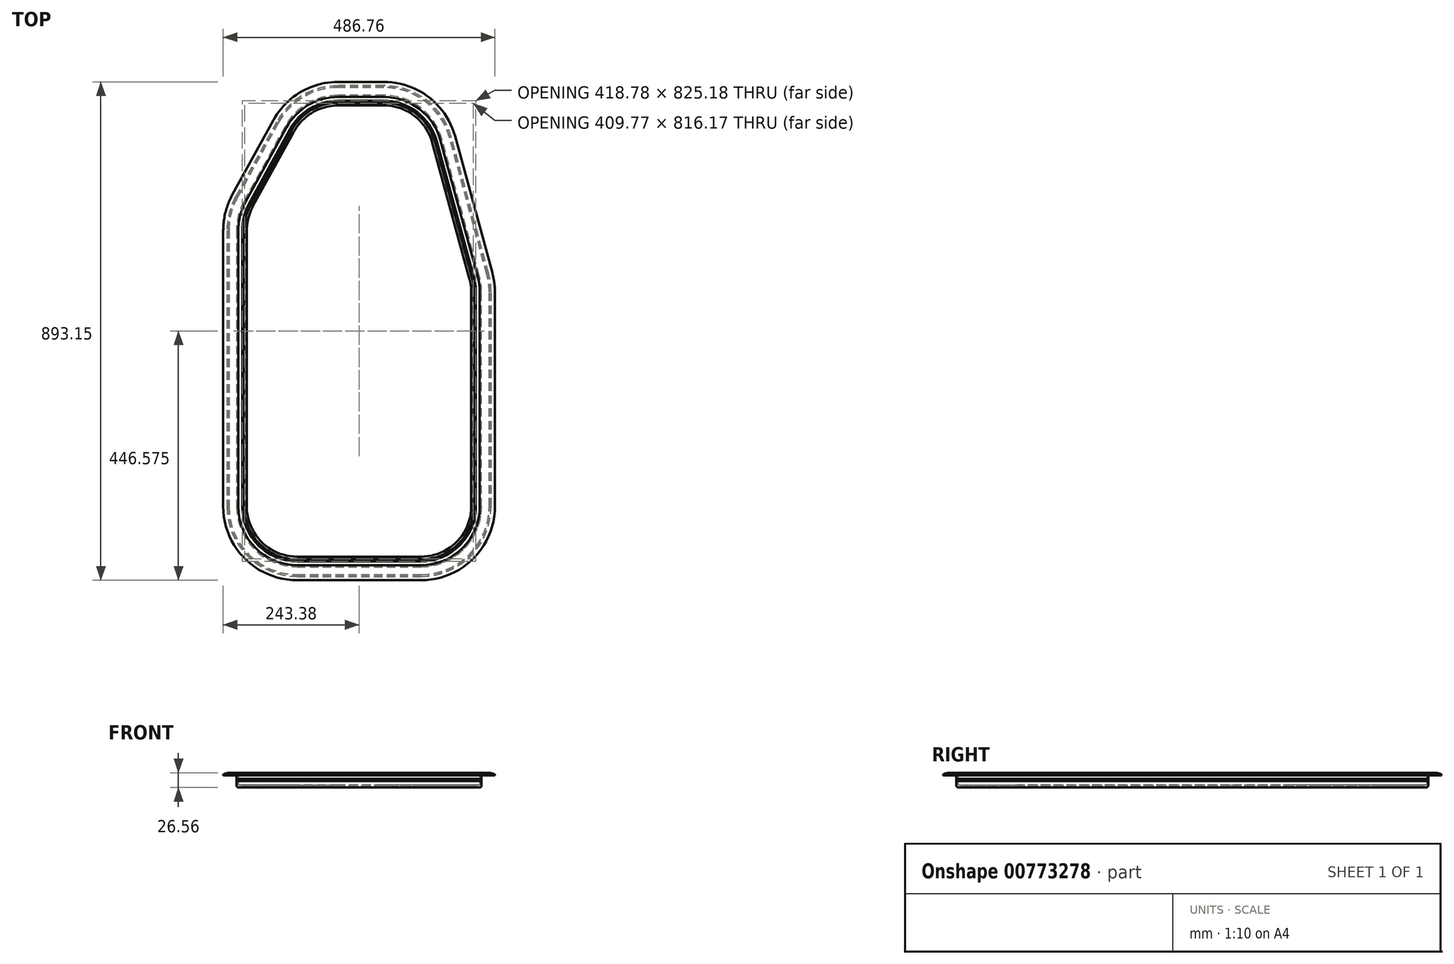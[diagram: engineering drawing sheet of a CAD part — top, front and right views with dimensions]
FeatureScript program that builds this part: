
annotation { "Feature Type Name" : "Feature", "Feature Type Description" : "" }
export const myFeature = defineFeature(function(context is Context, id is Id, definition is map)
    precondition{}
    {
        {
            var Q0;
            Q0=qCreatedBy(makeId("Top.planeOp"),FACE);
            var sketch = newSketch(context, id + "F0", { "sketchPlane" : qUnion([Q0])});
            skLineSegment(sketch, "E0.left", {"start": v(-444.5, 0) * mm, "end": v(-444.5, 494.82) * mm});
            skPoint(sketch, "E1.visualSharp", {"position": v(-444.5, 523.33) * mm});
            skPoint(sketch, "E2.visualSharp", {"position": v(-118.9, 850.9) * mm});
            skPoint(sketch, "E3.visualSharp", {"position": v(-351.5, 850.9) * mm});
            skPoint(sketch, "E4.visualSharp", {"position": v(-444.5, 510.04) * mm});
            skPoint(sketch, "E5.visualSharp", {"position": v(0, 0) * mm});
            skPoint(sketch, "E6.visualSharp", {"position": v(-444.5, 0) * mm});
            skArc(sketch, "E7.MirrorCS", {"start": v(-3.92, 413.28) * mm, "mid": v(-0.98, 398.79) * mm, "end": v(0, 384.03) * mm});
            skArc(sketch, "E8.MirrorCS", {"start": v(-444.5, 494.82) * mm, "mid": v(-441.01, 522.44) * mm, "end": v(-430.77, 548.32) * mm});
            skArc(sketch, "E9.MirrorCS", {"start": v(-333.38, -111.13) * mm, "mid": v(-411.95, -78.58) * mm, "end": v(-444.5, 0) * mm});
            skArc(sketch, "E10.MirrorCS", {"start": v(0, 0) * mm, "mid": v(-32.55, -78.58) * mm, "end": v(-111.13, -111.13) * mm});
            skArc(sketch, "E11.MirrorCS", {"start": v(-177.87, 739.77) * mm, "mid": v(-110.42, 716.97) * mm, "end": v(-70.66, 657.9) * mm});
            skArc(sketch, "E12.MirrorCS", {"start": v(-357.25, 682.16) * mm, "mid": v(-316.43, 724.3) * mm, "end": v(-259.85, 739.77) * mm});
            skLineSegment(sketch, "E13.MirrorCS", {"start": v(-70.66, 657.9) * mm, "end": v(-3.92, 413.28) * mm});
            skLineSegment(sketch, "E14.MirrorCS", {"start": v(-259.85, 739.77) * mm, "end": v(-177.87, 739.77) * mm});
            skLineSegment(sketch, "E15.MirrorCS", {"start": v(-430.77, 548.32) * mm, "end": v(-357.25, 682.16) * mm});
            skLineSegment(sketch, "E16.MirrorCS", {"start": v(0, 0) * mm, "end": v(0, 384.03) * mm});
            skLineSegment(sketch, "E17.MirrorCS", {"start": v(-333.38, -111.13) * mm, "end": v(-111.13, -111.13) * mm});
            skPoint(sketch, "E18.MirrorP", {"position": v(-770.1, 850.9) * mm});
            skPoint(sketch, "E19.MirrorP", {"position": v(-537.5, 850.9) * mm});
            skPoint(sketch, "E20.end.orphan", {"position": v(-711.13, 739.77) * mm});
            skPoint(sketch, "E2.filletArc.end.orphan", {"position": v(-629.15, 739.77) * mm});
            skPoint(sketch, "E21.end.orphan", {"position": v(-531.75, 682.16) * mm});
            skPoint(sketch, "E1.filletArc.end.orphan", {"position": v(-458.23, 548.32) * mm});
            skPoint(sketch, "E22.start.orphan", {"position": v(-818.34, 657.9) * mm});
            skPoint(sketch, "E4.filletArc.start.orphan", {"position": v(-885.08, 413.28) * mm});
            skPoint(sketch, "E0.right.end.orphan", {"position": v(-889, 384.03) * mm});
            skPoint(sketch, "E5.filletArc.start.orphan", {"position": v(-889, 0) * mm});
            skPoint(sketch, "E0.bottom.end.orphan", {"position": v(-777.88, -111.13) * mm});
            skPoint(sketch, "E6.filletArc.start.orphan", {"position": v(-555.62, -111.13) * mm});
            skSolve(sketch);
        }
        {
            var Q0;
            Q0=qCreatedBy(makeId("Front.planeOp"),FACE);
            var sketch = newSketch(context, id + "F1", { "sketchPlane" : qUnion([Q0])});
            skLineSegment(sketch, "E23", {"start": v(2.71, 8.36) * mm, "end": v(-2.71, 8.36) * mm});
            skLineSegment(sketch, "E24", {"start": v(-1.52, 13.28) * mm, "end": v(1.52, 13.28) * mm});
            skLineSegment(sketch, "E25.MirrorCS", {"start": v(-5.89, -8.71) * mm, "end": v(-12.86, -8.71) * mm});
            skLineSegment(sketch, "E26.MirrorCS", {"start": v(-5.89, -2.57) * mm, "end": v(-5.89, -8.71) * mm});
            skArc(sketch, "E27.MirrorCS", {"start": v(-2.71, -9.32) * mm, "mid": v(-3.87, -12.12) * mm, "end": v(-6.67, -13.28) * mm});
            skLineSegment(sketch, "E28.MirrorCS", {"start": v(-5.89, 0.6) * mm, "end": v(-5.89, -1.8) * mm});
            skArc(sketch, "E29.MirrorCS", {"start": v(-2.71, 1.4) * mm, "mid": v(-3.1, 1.78) * mm, "end": v(-2.71, 2.16) * mm});
            skArc(sketch, "E30.MirrorCS", {"start": v(-5.89, 1.37) * mm, "mid": v(-5.5, 1) * mm, "end": v(-5.89, 0.6) * mm});
            skArc(sketch, "E31.MirrorCS", {"start": v(-2.71, -1.78) * mm, "mid": v(-3.1, -1.4) * mm, "end": v(-2.71, -1.02) * mm});
            skLineSegment(sketch, "E32.MirrorCS", {"start": v(-2.71, -9.32) * mm, "end": v(-2.71, -1.78) * mm});
            skLineSegment(sketch, "E33.MirrorCS", {"start": v(-5.89, 8.92) * mm, "end": v(-5.89, 1.37) * mm});
            skArc(sketch, "E34.MirrorCS", {"start": v(-5.89, -1.8) * mm, "mid": v(-5.5, -2.18) * mm, "end": v(-5.89, -2.57) * mm});
            skArc(sketch, "E35.MirrorCS", {"start": v(-5.89, 8.92) * mm, "mid": v(-4.6, 12) * mm, "end": v(-1.52, 13.28) * mm});
            skLineSegment(sketch, "E36.MirrorCS", {"start": v(7.64, 13.28) * mm, "end": v(-1.52, 13.28) * mm});
            skLineSegment(sketch, "E37.MirrorCS", {"start": v(-2.71, 2.16) * mm, "end": v(-2.71, 8.36) * mm});
            skLineSegment(sketch, "E38.MirrorCS", {"start": v(-2.71, 8.36) * mm, "end": v(10.84, 8.36) * mm});
            skArc(sketch, "E39.MirrorCS", {"start": v(10.84, 8.36) * mm, "mid": v(11.22, 8.74) * mm, "end": v(11.6, 8.36) * mm});
            skLineSegment(sketch, "E40.MirrorCS", {"start": v(-2.71, 8.36) * mm, "end": v(2.71, 8.36) * mm});
            skArc(sketch, "E41.MirrorCS", {"start": v(13.95, 8.36) * mm, "mid": v(14.2, 8.61) * mm, "end": v(14.46, 8.36) * mm});
            skArc(sketch, "E42.MirrorCS", {"start": v(7.64, 13.28) * mm, "mid": v(14.17, 12.6) * mm, "end": v(20.43, 10.6) * mm});
            skLineSegment(sketch, "E43.MirrorCS", {"start": v(14.46, 8.36) * mm, "end": v(19.96, 8.36) * mm});
            skLineSegment(sketch, "E44.MirrorCS", {"start": v(11.6, 8.36) * mm, "end": v(13.95, 8.36) * mm});
            skArc(sketch, "E45.MirrorCS", {"start": v(20.43, 10.6) * mm, "mid": v(21.1, 9.28) * mm, "end": v(19.96, 8.36) * mm});
            skLineSegment(sketch, "E46.MirrorCS", {"start": v(-12.86, -8.71) * mm, "end": v(-12.86, -9.73) * mm});
            skLineSegment(sketch, "E47.MirrorCS", {"start": v(-17.37, -9.73) * mm, "end": v(-16.29, -9.73) * mm});
            skLineSegment(sketch, "E48.MirrorCS", {"start": v(-12.86, -9.73) * mm, "end": v(-11.78, -9.73) * mm});
            skLineSegment(sketch, "E49.MirrorCS", {"start": v(-16.29, -9.73) * mm, "end": v(-16.29, -8.71) * mm});
            skLineSegment(sketch, "E50.MirrorCS", {"start": v(-11.78, -9.73) * mm, "end": v(-11.78, -11.38) * mm});
            skArc(sketch, "E51.MirrorCS", {"start": v(-21.07, -9.32) * mm, "mid": v(-21.07, -8.92) * mm, "end": v(-20.72, -8.71) * mm});
            skLineSegment(sketch, "E52.MirrorCS", {"start": v(-17.37, -11.38) * mm, "end": v(-17.37, -9.73) * mm});
            skLineSegment(sketch, "E53.MirrorCS", {"start": v(-11.78, -11.38) * mm, "end": v(-17.37, -11.38) * mm});
            skLineSegment(sketch, "E54.MirrorCS", {"start": v(-16.29, -8.71) * mm, "end": v(-20.72, -8.71) * mm});
            skLineSegment(sketch, "E55.MirrorCS", {"start": v(-21.07, -9.32) * mm, "end": v(-19.47, -12.1) * mm});
            skArc(sketch, "E56.MirrorCS", {"start": v(-17.4, -13.28) * mm, "mid": v(-18.6, -12.96) * mm, "end": v(-19.47, -12.1) * mm});
            skLineSegment(sketch, "E57.MirrorCS", {"start": v(-17.4, -13.28) * mm, "end": v(-6.67, -13.28) * mm});
            skLineSegment(sketch, "E58.MirrorCS", {"start": v(-2.71, -1.02) * mm, "end": v(-2.71, 1.4) * mm});
            skPoint(sketch, "E59.end.orphan", {"position": v(-20.43, 10.6) * mm});
            skPoint(sketch, "E59.start.orphan", {"position": v(-7.64, 13.28) * mm});
            skPoint(sketch, "E60.end.orphan", {"position": v(-19.96, 8.36) * mm});
            skPoint(sketch, "E61.start.orphan", {"position": v(-14.46, 8.36) * mm});
            skPoint(sketch, "E62.start.orphan", {"position": v(-13.95, 8.36) * mm});
            skPoint(sketch, "E63.start.orphan", {"position": v(-11.6, 8.36) * mm});
            skPoint(sketch, "E64.start.orphan", {"position": v(-10.84, 8.36) * mm});
            skPoint(sketch, "E65.end.orphan", {"position": v(1.52, 13.28) * mm});
            skPoint(sketch, "E65.start.orphan", {"position": v(5.89, 8.92) * mm});
            skLineSegment(sketch, "E66.trimOffspring", {"start": v(5.89, 8.36) * mm, "end": v(10.84, 8.36) * mm});
            skPoint(sketch, "E67.end.orphan", {"position": v(2.71, 8.36) * mm});
            skPoint(sketch, "E67.start.orphan", {"position": v(2.71, 2.16) * mm});
            skPoint(sketch, "E68.orphan", {"position": v(5.89, 1.37) * mm});
            skPoint(sketch, "E69.start.orphan", {"position": v(2.71, 1.4) * mm});
            skPoint(sketch, "E70.end.orphan", {"position": v(5.89, 0.6) * mm});
            skPoint(sketch, "E71.start.orphan", {"position": v(2.71, -1.02) * mm});
            skPoint(sketch, "E72.end.orphan", {"position": v(5.89, -1.8) * mm});
            skPoint(sketch, "E73.start.orphan", {"position": v(2.71, -1.78) * mm});
            skPoint(sketch, "E74.end.orphan", {"position": v(5.89, -2.57) * mm});
            skSolve(sketch);
        }
        {
            var Q0;
            Q0 = qSketchRegion(id + "F1", true);
            var Q1;
            Q1 = qConstructionFilter(qBodyType(qCreatedBy(id + "F0" ,EDGE), BodyType.WIRE), ConstructionObject.NO);
            sweep(context, id + "F2", {"profiles" : qUnion([Q0]), "path" : qUnion([Q1])});
        }
    });
